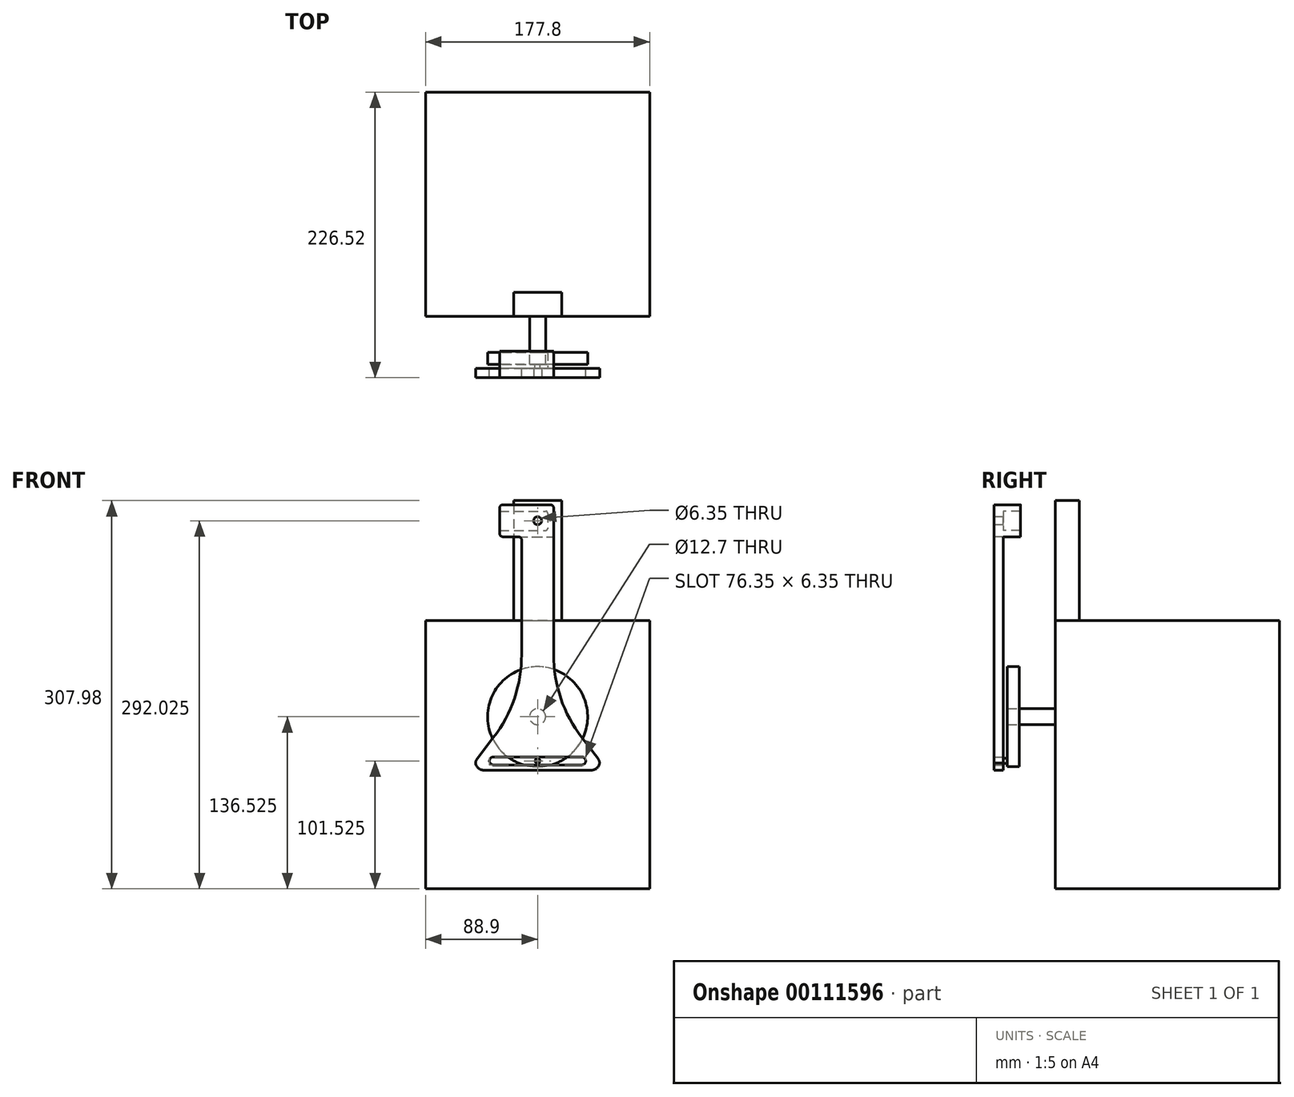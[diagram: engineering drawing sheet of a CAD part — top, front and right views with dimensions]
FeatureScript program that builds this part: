
annotation { "Feature Type Name" : "Feature", "Feature Type Description" : "" }
export const myFeature = defineFeature(function(context is Context, id is Id, definition is map)
    precondition{}
    {
        {
            var Q0;
            Q0=qCreatedBy(makeId("Top.planeOp"),FACE);
            var sketch = newSketch(context, id + "F0", { "sketchPlane" : qUnion([Q0])});
            skLineSegment(sketch, "E0.bottom", {"start": v(-88.9, -88.9) * mm, "end": v(88.9, -88.9) * mm});
            skLineSegment(sketch, "E0.top", {"start": v(-88.9, 88.9) * mm, "end": v(88.9, 88.9) * mm});
            skLineSegment(sketch, "E0.left", {"start": v(-88.9, -88.9) * mm, "end": v(-88.9, 88.9) * mm});
            skLineSegment(sketch, "E0.right", {"start": v(88.9, -88.9) * mm, "end": v(88.9, 88.9) * mm});
            skPoint(sketch, "E0.middle", {"position": v(0, 0) * mm});
            skSolve(sketch);
        }
        {
            var Q0;
            Q0 = qSketchRegion(id + "F0", true);
            extrude(context, id + "F1", {"entities" : qUnion([Q0]), "depth" : 212.72 * mm});
        }
        {
            var Q0;
            Q0=makeQuery(id+"F1.opExtrude","CAP_FACE",FACE,{"disambiguationData":[OSD([sQuery(id+"F0.wireOp",EDGE,"E0.bottom"),sQuery(id+"F0.wireOp",EDGE,"E0.top"),sQuery(id+"F0.wireOp",EDGE,"E0.left"),sQuery(id+"F0.wireOp",EDGE,"E0.right")])],"isStart":false});
            var sketch = newSketch(context, id + "F2", { "sketchPlane" : qUnion([Q0])});
            skLineSegment(sketch, "E1.bottom", {"start": v(19.05, -88.9) * mm, "end": v(-19.05, -88.9) * mm});
            skLineSegment(sketch, "E1.top", {"start": v(19.05, -69.85) * mm, "end": v(-19.05, -69.85) * mm});
            skLineSegment(sketch, "E1.left", {"start": v(19.05, -88.9) * mm, "end": v(19.05, -69.85) * mm});
            skLineSegment(sketch, "E1.right", {"start": v(-19.05, -88.9) * mm, "end": v(-19.05, -69.85) * mm});
            skPoint(sketch, "E2", {"position": v(0, -88.9) * mm});
            skSolve(sketch);
        }
        {
            var Q0;
            Q0 = qSketchRegion(id + "F2", true);
            extrude(context, id + "F3", {"entities" : qUnion([Q0]), "depth" : 95.25 * mm});
        }
        {
            var Q0;
            Q0=makeQuery(id+"F1.opExtrude","SWEPT_FACE",FACE,{"disambiguationData":[OSD([sQuery(id+"F0.wireOp",EDGE,"E0.bottom")])]});
            var sketch = newSketch(context, id + "F4", { "sketchPlane" : qUnion([Q0])});
            skCircle(sketch, "E3", {"center": v(0, 136.53) * mm, "radius": 6.35 * mm});
            skSolve(sketch);
        }
        {
            var Q0;
            Q0 = qSketchRegion(id + "F4", true);
            extrude(context, id + "F5", {"entities" : qUnion([Q0]), "operationType" : NewBodyOperationType.ADD, "depth" : 38.1 * mm});
        }
        {
            var Q0;
            Q0=makeQuery(id+"F5.opExtrude","CAP_FACE",FACE,{"disambiguationData":[OSD([sQuery(id+"F4.wireOp",EDGE,"E3")])],"isStart":false});
            var sketch = newSketch(context, id + "F6", { "sketchPlane" : qUnion([Q0])});
            skCircle(sketch, "E4", {"center": v(0, 136.53) * mm, "radius": 39.69 * mm});
            skSolve(sketch);
        }
        {
            var Q0;
            Q0 = qSketchRegion(id + "F6", true);
            extrude(context, id + "F7", {"entities" : qUnion([Q0]), "oppositeDirection" : true, "depth" : 9.52 * mm});
        }
        {
            var Q0;
            Q0=makeQuery(id+"F1.opExtrude","SWEPT_BODY",BODY,{"disambiguationData":[OSD([sQuery(id+"F0.wireOp",EDGE,"E0.bottom"),sQuery(id+"F0.wireOp",EDGE,"E0.top"),sQuery(id+"F0.wireOp",EDGE,"E0.left"),sQuery(id+"F0.wireOp",EDGE,"E0.right")])]});
            var Q1;
            Q1=makeQuery(id+"F7.opExtrude","SWEPT_BODY",BODY,{"disambiguationData":[OSD([sQuery(id+"F6.wireOp",EDGE,"E4")])]});
            booleanBodies(context, id + "F8", {"operationType" : BooleanOperationType.SUBTRACTION, "tools" : qUnion([Q0]), "targets" : qUnion([Q1]), "keepTools" : true});
        }
        {
            var Q0;
            Q0=makeQuery(id+"F7.opExtrude","CAP_FACE",FACE,{"disambiguationData":[OSD([sQuery(id+"F6.wireOp",EDGE,"E4")])],"isStart":true});
            var sketch = newSketch(context, id + "F9", { "sketchPlane" : qUnion([Q0])});
            skCircle(sketch, "E5", {"center": v(0, 101.53) * mm, "radius": 1.97 * mm});
            skPoint(sketch, "E6", {"position": v(0, 136.53) * mm});
            skSolve(sketch);
        }
        {
            var Q0;
            Q0 = qSketchRegion(id + "F9", true);
            extrude(context, id + "F10", {"entities" : qUnion([Q0]), "operationType" : NewBodyOperationType.ADD, "depth" : 3.3 * mm});
        }
        {
            var Q0;
            Q0=makeQuery(id+"F10.opExtrude","CAP_FACE",FACE,{"disambiguationData":[OSD([sQuery(id+"F9.wireOp",EDGE,"E5")])],"isStart":false});
            var sketch = newSketch(context, id + "F11", { "sketchPlane" : qUnion([Q0])});
            skPoint(sketch, "E7", {"position": v(0, 101.53) * mm});
            skLineSegment(sketch, "E8.bottom", {"start": v(35, 104.7) * mm, "end": v(-35, 104.7) * mm});
            skLineSegment(sketch, "E8.top", {"start": v(35, 98.35) * mm, "end": v(-35, 98.35) * mm});
            skLineSegment(sketch, "E9.top", {"start": v(49.21, 94.22) * mm, "end": v(-49.21, 94.22) * mm});
            skLineSegment(sketch, "E9.left", {"start": v(49.21, 101.52) * mm, "end": v(49.21, 94.22) * mm});
            skLineSegment(sketch, "E9.right", {"start": v(-49.21, 101.52) * mm, "end": v(-49.21, 94.22) * mm});
            skLineSegment(sketch, "E10", {"start": v(-49.21, 101.52) * mm, "end": v(-12.7, 149.1) * mm});
            skLineSegment(sketch, "E11", {"start": v(12.7, 149.1) * mm, "end": v(49.21, 101.52) * mm});
            skLineSegment(sketch, "E12.top", {"start": v(12.7, 304.73) * mm, "end": v(-12.7, 304.73) * mm});
            skLineSegment(sketch, "E12.left", {"start": v(12.7, 149.1) * mm, "end": v(12.7, 304.73) * mm});
            skLineSegment(sketch, "E12.right", {"start": v(-12.7, 149.1) * mm, "end": v(-12.7, 304.73) * mm});
            skPoint(sketch, "E12.middle", {"position": v(0, 226.92) * mm});
            skPoint(sketch, "E13.orphan", {"position": v(0, 165.66) * mm});
            skPoint(sketch, "E14.orphan", {"position": v(49.21, 108.83) * mm});
            skPoint(sketch, "E15.orphan", {"position": v(-49.21, 108.83) * mm});
            skArc(sketch, "E16", {"start": v(-35, 104.7) * mm, "mid": v(-38.18, 101.52) * mm, "end": v(-35, 98.35) * mm});
            skPoint(sketch, "E16.first.point", {"position": v(-35, 104.7) * mm});
            skPoint(sketch, "E16.second.point", {"position": v(-38.18, 101.53) * mm});
            skPoint(sketch, "E16.third.point", {"position": v(-35, 98.35) * mm});
            skArc(sketch, "E17", {"start": v(35, 98.35) * mm, "mid": v(38.18, 101.52) * mm, "end": v(35, 104.7) * mm});
            skPoint(sketch, "E17.first.point", {"position": v(35, 104.7) * mm});
            skPoint(sketch, "E17.second.point", {"position": v(38.18, 101.53) * mm});
            skPoint(sketch, "E17.third.point", {"position": v(35, 98.35) * mm});
            skPoint(sketch, "E18.orphan", {"position": v(-38.18, 104.7) * mm});
            skPoint(sketch, "E19.orphan", {"position": v(-38.18, 98.35) * mm});
            skPoint(sketch, "E20.orphan", {"position": v(38.18, 104.7) * mm});
            skPoint(sketch, "E8.left.end.orphan", {"position": v(38.18, 98.35) * mm});
            skSolve(sketch);
        }
        {
            var Q0;
            Q0 = qSketchRegion(id + "F11", true);
            extrude(context, id + "F12", {"entities" : qUnion([Q0]), "depth" : 7.32 * mm});
        }
        {
            var Q0;
            Q0=makeQuery(id+"F12.opExtrude","CAP_FACE",FACE,{"disambiguationData":[OSD([sQuery(id+"F11.wireOp",EDGE,"E8.bottom"),sQuery(id+"F11.wireOp",EDGE,"E8.top"),sQuery(id+"F11.wireOp",EDGE,"E8.left"),sQuery(id+"F11.wireOp",EDGE,"E8.right"),sQuery(id+"F11.wireOp",EDGE,"E9.top"),sQuery(id+"F11.wireOp",EDGE,"E9.left"),sQuery(id+"F11.wireOp",EDGE,"E9.right"),sQuery(id+"F11.wireOp",EDGE,"E10"),sQuery(id+"F11.wireOp",EDGE,"E11"),sQuery(id+"F11.wireOp",EDGE,"E12.top"),sQuery(id+"F11.wireOp",EDGE,"E12.left"),sQuery(id+"F11.wireOp",EDGE,"E12.right")])],"isStart":true});
            var sketch = newSketch(context, id + "F13", { "sketchPlane" : qUnion([Q0])});
            skLineSegment(sketch, "E21.0", {"start": v(12.7, 304.73) * mm, "end": v(-12.7, 304.73) * mm});
            skLineSegment(sketch, "E21.1", {"start": v(12.7, 304.73) * mm, "end": v(12.7, 149.1) * mm});
            skLineSegment(sketch, "E21.2", {"start": v(12.7, 149.1) * mm, "end": v(49.21, 101.52) * mm});
            skLineSegment(sketch, "E21.3", {"start": v(49.21, 94.22) * mm, "end": v(49.21, 101.52) * mm});
            skLineSegment(sketch, "E21.4", {"start": v(49.21, 94.22) * mm, "end": v(-49.21, 94.22) * mm});
            skLineSegment(sketch, "E21.5", {"start": v(-49.21, 94.22) * mm, "end": v(-49.21, 101.52) * mm});
            skLineSegment(sketch, "E21.6", {"start": v(-49.21, 101.53) * mm, "end": v(-12.7, 149.1) * mm});
            skLineSegment(sketch, "E21.7", {"start": v(-12.7, 304.73) * mm, "end": v(-12.7, 149.1) * mm});
            skSolve(sketch);
        }
        {
            var Q0;
            Q0=makeQuery(id+"FnXf4SUWYjh47XK_4.boolean.opBoolean","MERGE",EDGE,{"derivedFrom":[makeQuery(id+"F12.opExtrude","SWEPT_EDGE",EDGE,{"disambiguationData":[OSD([sQuery(id+"F11.wireOp",EDGE,"E9.left"),sQuery(id+"F11.wireOp",EDGE,"E11")])]}),makeQuery(id+"FnXf4SUWYjh47XK_4.opExtrude","SWEPT_EDGE",EDGE,{"disambiguationData":[OSD([sQuery(id+"F13.wireOp",EDGE,"E21.5"),sQuery(id+"F13.wireOp",EDGE,"E21.6")])]})]});
            var Q1;
            Q1=makeQuery(id+"FnXf4SUWYjh47XK_4.boolean.opBoolean","MERGE",EDGE,{"derivedFrom":[makeQuery(id+"F12.opExtrude","SWEPT_EDGE",EDGE,{"disambiguationData":[OSD([sQuery(id+"F11.wireOp",EDGE,"E9.top"),sQuery(id+"F11.wireOp",EDGE,"E9.left")])]}),makeQuery(id+"FnXf4SUWYjh47XK_4.opExtrude","SWEPT_EDGE",EDGE,{"disambiguationData":[OSD([sQuery(id+"F13.wireOp",EDGE,"E21.4"),sQuery(id+"F13.wireOp",EDGE,"E21.5")])]})]});
            var Q2;
            Q2=makeQuery(id+"FnXf4SUWYjh47XK_4.boolean.opBoolean","MERGE",EDGE,{"derivedFrom":[makeQuery(id+"F12.opExtrude","SWEPT_EDGE",EDGE,{"disambiguationData":[OSD([sQuery(id+"F11.wireOp",EDGE,"E9.top"),sQuery(id+"F11.wireOp",EDGE,"E9.right")])]}),makeQuery(id+"FnXf4SUWYjh47XK_4.opExtrude","SWEPT_EDGE",EDGE,{"disambiguationData":[OSD([sQuery(id+"F13.wireOp",EDGE,"E21.3"),sQuery(id+"F13.wireOp",EDGE,"E21.4")])]})]});
            var Q3;
            Q3=makeQuery(id+"FnXf4SUWYjh47XK_4.boolean.opBoolean","MERGE",EDGE,{"derivedFrom":[makeQuery(id+"F12.opExtrude","SWEPT_EDGE",EDGE,{"disambiguationData":[OSD([sQuery(id+"F11.wireOp",EDGE,"E9.right"),sQuery(id+"F11.wireOp",EDGE,"E10")])]}),makeQuery(id+"FnXf4SUWYjh47XK_4.opExtrude","SWEPT_EDGE",EDGE,{"disambiguationData":[OSD([sQuery(id+"F13.wireOp",EDGE,"E21.2"),sQuery(id+"F13.wireOp",EDGE,"E21.3")])]})]});
            fillet(context, id + "F14", {"entities" : qUnion([Q0, Q1, Q2, Q3]), "radius" : 6.35 * mm, "tangentPropagation" : true, "allowEdgeOverflow" : false});
        }
        {
            var Q0;
            Q0=makeQuery(id+"FnXf4SUWYjh47XK_4.boolean.opBoolean","MERGE",EDGE,{"derivedFrom":[makeQuery(id+"F12.opExtrude","SWEPT_EDGE",EDGE,{"disambiguationData":[OSD([sQuery(id+"F11.wireOp",EDGE,"E10"),sQuery(id+"F11.wireOp",EDGE,"E12.right")])]}),makeQuery(id+"FnXf4SUWYjh47XK_4.opExtrude","SWEPT_EDGE",EDGE,{"disambiguationData":[OSD([sQuery(id+"F13.wireOp",EDGE,"E21.1"),sQuery(id+"F13.wireOp",EDGE,"E21.2")])]})]});
            var Q1;
            Q1=makeQuery(id+"FnXf4SUWYjh47XK_4.boolean.opBoolean","MERGE",EDGE,{"derivedFrom":[makeQuery(id+"F12.opExtrude","SWEPT_EDGE",EDGE,{"disambiguationData":[OSD([sQuery(id+"F11.wireOp",EDGE,"E11"),sQuery(id+"F11.wireOp",EDGE,"E12.left")])]}),makeQuery(id+"FnXf4SUWYjh47XK_4.opExtrude","SWEPT_EDGE",EDGE,{"disambiguationData":[OSD([sQuery(id+"F13.wireOp",EDGE,"E21.6"),sQuery(id+"F13.wireOp",EDGE,"E21.7")])]})]});
            fillet(context, id + "F15", {"entities" : qUnion([Q0, Q1]), "radius" : 107.95 * mm, "tangentPropagation" : true, "allowEdgeOverflow" : false});
        }
        {
            var Q0;
            Q0=makeQuery(id+"F12.opExtrude","CAP_FACE",FACE,{"disambiguationData":[OSD([sQuery(id+"F11.wireOp",EDGE,"E8.bottom"),sQuery(id+"F11.wireOp",EDGE,"E8.top"),sQuery(id+"F11.wireOp",EDGE,"E9.top"),sQuery(id+"F11.wireOp",EDGE,"E9.left"),sQuery(id+"F11.wireOp",EDGE,"E9.right"),sQuery(id+"F11.wireOp",EDGE,"E10"),sQuery(id+"F11.wireOp",EDGE,"E11"),sQuery(id+"F11.wireOp",EDGE,"E12.top"),sQuery(id+"F11.wireOp",EDGE,"E12.left"),sQuery(id+"F11.wireOp",EDGE,"E12.right"),sQuery(id+"F11.wireOp",EDGE,"E16"),sQuery(id+"F11.wireOp",EDGE,"E17")])],"isStart":false});
            var sketch = newSketch(context, id + "F16", { "sketchPlane" : qUnion([Q0])});
            skCircle(sketch, "E22", {"center": v(0, 292.03) * mm, "radius": 3.18 * mm});
            skPoint(sketch, "E23", {"position": v(0, 101.53) * mm});
            skSolve(sketch);
        }
        {
            var Q0;
            Q0 = qSketchRegion(id + "F16", true);
            extrude(context, id + "F17", {"entities" : qUnion([Q0]), "operationType" : NewBodyOperationType.REMOVE, "endBound" : BoundingType.UP_TO_NEXT, "oppositeDirection" : true, "depth" : 25.4 * mm});
        }
        {
            var Q0;
            Q0=makeQuery(id+"F12.opExtrude","CAP_FACE",FACE,{"disambiguationData":[OSD([sQuery(id+"F11.wireOp",EDGE,"E8.bottom"),sQuery(id+"F11.wireOp",EDGE,"E8.top"),sQuery(id+"F11.wireOp",EDGE,"E9.top"),sQuery(id+"F11.wireOp",EDGE,"E9.left"),sQuery(id+"F11.wireOp",EDGE,"E9.right"),sQuery(id+"F11.wireOp",EDGE,"E10"),sQuery(id+"F11.wireOp",EDGE,"E11"),sQuery(id+"F11.wireOp",EDGE,"E12.top"),sQuery(id+"F11.wireOp",EDGE,"E12.left"),sQuery(id+"F11.wireOp",EDGE,"E12.right"),sQuery(id+"F11.wireOp",EDGE,"E16"),sQuery(id+"F11.wireOp",EDGE,"E17")])],"isStart":true});
            var sketch = newSketch(context, id + "F18", { "sketchPlane" : qUnion([Q0])});
            skLineSegment(sketch, "E24.bottom", {"start": v(30.1, 299.65) * mm, "end": v(-6.41, 299.65) * mm});
            skLineSegment(sketch, "E24.top", {"start": v(30.1, 284.4) * mm, "end": v(-6.41, 284.4) * mm});
            skLineSegment(sketch, "E24.right", {"start": v(-8, 298.06) * mm, "end": v(-8, 286) * mm});
            skPoint(sketch, "E24.middle", {"position": v(0, 292.03) * mm});
            skLineSegment(sketch, "E25.0", {"start": v(30.1, 279.33) * mm, "end": v(-12.7, 279.33) * mm});
            skLineSegment(sketch, "E25.1", {"start": v(-12.7, 304.73) * mm, "end": v(-12.7, 279.33) * mm});
            skLineSegment(sketch, "E25.2", {"start": v(30.1, 304.73) * mm, "end": v(-12.7, 304.73) * mm});
            skLineSegment(sketch, "E26", {"start": v(30.1, 304.73) * mm, "end": v(30.1, 299.65) * mm});
            skLineSegment(sketch, "E27", {"start": v(30.1, 284.4) * mm, "end": v(30.1, 279.33) * mm});
            skPoint(sketch, "E28.visualSharp", {"position": v(-8, 299.65) * mm});
            skArc(sketch, "E28.filletArc", {"start": v(-6.41, 299.65) * mm, "mid": v(-7.54, 299.18) * mm, "end": v(-8, 298.06) * mm});
            skPoint(sketch, "E29.visualSharp", {"position": v(-8, 284.4) * mm});
            skArc(sketch, "E29.filletArc", {"start": v(-8, 286) * mm, "mid": v(-7.54, 284.87) * mm, "end": v(-6.41, 284.4) * mm});
            skSolve(sketch);
        }
        {
            var Q0;
            Q0 = qSketchRegion(id + "F18", true);
            var Q1;
            Q1=makeQuery(id+"F12.opExtrude","CAP_FACE",FACE,{"disambiguationData":[OSD([sQuery(id+"F11.wireOp",EDGE,"E8.bottom"),sQuery(id+"F11.wireOp",EDGE,"E8.top"),sQuery(id+"F11.wireOp",EDGE,"E9.top"),sQuery(id+"F11.wireOp",EDGE,"E9.left"),sQuery(id+"F11.wireOp",EDGE,"E9.right"),sQuery(id+"F11.wireOp",EDGE,"E10"),sQuery(id+"F11.wireOp",EDGE,"E11"),sQuery(id+"F11.wireOp",EDGE,"E12.top"),sQuery(id+"F11.wireOp",EDGE,"E12.left"),sQuery(id+"F11.wireOp",EDGE,"E12.right"),sQuery(id+"F11.wireOp",EDGE,"E16"),sQuery(id+"F11.wireOp",EDGE,"E17")])],"isStart":false});
            extrude(context, id + "F19", {"entities" : qUnion([Q0]), "operationType" : NewBodyOperationType.ADD, "depth" : 13.72 * mm});
        }
        {
            var Q0;
            {var subQ0=sQuery(id+"F18.wireOp",EDGE,"E25.1");var subQ1=sQuery(id+"F18.wireOp",EDGE,"E24.right");var subQ2=sQuery(id+"F18.wireOp",EDGE,"E24.bottom");var subQ5=sQuery(id+"F11.wireOp",EDGE,"E12.top");var subQ6=sQuery(id+"F18.wireOp",EDGE,"E26");var subQ7=sQuery(id+"F18.wireOp",EDGE,"E25.2");var subQ8=sQuery(id+"F18.wireOp",EDGE,"E25.0");var subQ9=sQuery(id+"F18.wireOp",EDGE,"E28.filletArc");var subQ10=sQuery(id+"F18.wireOp",EDGE,"E29.filletArc");Q0=makeQuery(id+"F19.boolean.opBoolean","SPLIT",FACE,{"disambiguationData":[TD([makeQuery(id+"F12.opExtrude","SWEPT_FACE",FACE,{"disambiguationData":[OSD([subQ5])]})])],"derivedFrom":makeQuery(id+"F19.opExtrude","CAP_FACE",FACE,{"disambiguationData":[OSD([subQ2,sQuery(id+"F18.wireOp",EDGE,"E24.top"),subQ1,subQ8,subQ0,subQ7,subQ6,sQuery(id+"F18.wireOp",EDGE,"E27"),subQ9,subQ10])],"isStart":true})});}
            var sketch = newSketch(context, id + "F20", { "sketchPlane" : qUnion([Q0])});
            skLineSegment(sketch, "E30", {"start": v(12.7, 279.33) * mm, "end": v(12.7, 304.73) * mm});
            skLineSegment(sketch, "E31", {"start": v(12.7, 304.73) * mm, "end": v(-30.1, 304.73) * mm});
            skLineSegment(sketch, "E32", {"start": v(-30.1, 304.73) * mm, "end": v(-30.1, 279.33) * mm});
            skLineSegment(sketch, "E33", {"start": v(-30.1, 279.33) * mm, "end": v(12.7, 279.33) * mm});
            skCircle(sketch, "E34.0", {"center": v(0, 292.03) * mm, "radius": 3.18 * mm});
            skSolve(sketch);
        }
        {
            var Q0;
            Q0 = qSketchRegion(id + "F20", true);
            var Q1;
            Q1=makeQuery(id+"F12.opExtrude","CAP_FACE",FACE,{"disambiguationData":[OSD([sQuery(id+"F11.wireOp",EDGE,"E8.bottom"),sQuery(id+"F11.wireOp",EDGE,"E8.top"),sQuery(id+"F11.wireOp",EDGE,"E9.top"),sQuery(id+"F11.wireOp",EDGE,"E9.left"),sQuery(id+"F11.wireOp",EDGE,"E9.right"),sQuery(id+"F11.wireOp",EDGE,"E10"),sQuery(id+"F11.wireOp",EDGE,"E11"),sQuery(id+"F11.wireOp",EDGE,"E12.top"),sQuery(id+"F11.wireOp",EDGE,"E12.left"),sQuery(id+"F11.wireOp",EDGE,"E12.right"),sQuery(id+"F11.wireOp",EDGE,"E16"),sQuery(id+"F11.wireOp",EDGE,"E17")])],"isStart":false});
            extrude(context, id + "F21", {"entities" : qUnion([Q0]), "operationType" : NewBodyOperationType.ADD, "endBound" : BoundingType.UP_TO_SURFACE, "endBoundEntityFace" : qUnion([Q1]), "depth" : 25.4 * mm});
        }
        {
            var Q0;
            Q0=makeQuery(id+"F21.boolean.opBoolean","INTERSECT",EDGE,{"derivedFrom":[makeQuery(id+"F12.opExtrude","SWEPT_FACE",FACE,{"disambiguationData":[OSD([sQuery(id+"F11.wireOp",EDGE,"E12.right")])]}),makeQuery(id+"F21.opExtrude","SWEPT_FACE",FACE,{"disambiguationData":[OSD([sQuery(id+"F20.wireOp",EDGE,"E33")])]})]});
            var Q1;
            Q1=makeQuery(id+"F21.boolean.opBoolean","MERGE",EDGE,{"derivedFrom":[makeQuery(id+"F19.opExtrude","SWEPT_EDGE",EDGE,{"disambiguationData":[OSD([sQuery(id+"F18.wireOp",EDGE,"E25.0"),sQuery(id+"F18.wireOp",EDGE,"E27")])]}),makeQuery(id+"F21.opExtrude","SWEPT_EDGE",EDGE,{"disambiguationData":[OSD([sQuery(id+"F20.wireOp",EDGE,"E32"),sQuery(id+"F20.wireOp",EDGE,"E33")])]})]});
            var Q2;
            Q2=makeQuery(id+"F21.boolean.opBoolean","MERGE",EDGE,{"derivedFrom":[makeQuery(id+"F19.opExtrude","SWEPT_EDGE",EDGE,{"disambiguationData":[OSD([sQuery(id+"F18.wireOp",EDGE,"E25.2"),sQuery(id+"F18.wireOp",EDGE,"E26")])]}),makeQuery(id+"F21.opExtrude","SWEPT_EDGE",EDGE,{"disambiguationData":[OSD([sQuery(id+"F20.wireOp",EDGE,"E31"),sQuery(id+"F20.wireOp",EDGE,"E32")])]})]});
            var Q3;
            Q3=makeQuery(id+"F19.boolean.opBoolean","MERGE",EDGE,{"derivedFrom":[makeQuery(id+"F12.opExtrude","SWEPT_EDGE",EDGE,{"disambiguationData":[OSD([sQuery(id+"F11.wireOp",EDGE,"E12.top"),sQuery(id+"F11.wireOp",EDGE,"E12.left")])]}),makeQuery(id+"F19.opExtrude","SWEPT_EDGE",EDGE,{"disambiguationData":[OSD([sQuery(id+"F18.wireOp",EDGE,"E25.1"),sQuery(id+"F18.wireOp",EDGE,"E25.2")])]})]});
            fillet(context, id + "F22", {"entities" : qUnion([Q0, Q1, Q2, Q3]), "radius" : 2.54 * mm, "tangentPropagation" : true, "allowEdgeOverflow" : false});
        }
    });
